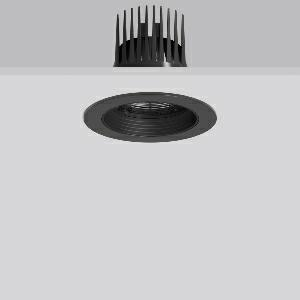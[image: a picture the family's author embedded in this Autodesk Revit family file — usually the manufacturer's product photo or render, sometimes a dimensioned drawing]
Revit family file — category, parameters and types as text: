
# Revit family: heledon_maxi_e_901769_003_c5fb
name_source: partatom
category: Lighting Fixtures
units: mm (PartAtom-declared; Revit-internal decimal feet)

## family parameters
Cut with Voids When Loaded = No
Host = Face
Light Source = No
Part Type = Normal
Room Calculation Point = No
Round Connector Dimension = Use Diameter
Shared = No

## types (1)
- HELEDON maxi E (1 x LED Modul 930, 3600 lm, 3000)
    Apparent Load = 35 VA
    Approval mark = CE
    CIE Flux Codes = 96 100 100 100 100
    Color Rendering = 90
    Color Temperature = 3000
    Default Elevation = 1800 mm
    Description = Series: HELEDON maxi
Round recessed downlight. Housing: die-cast aluminium, powder-coated. Black plastic ring and recessed LED to prevent glare from the side. Optical assembly with lens made of plastic (polycarbonate) for the best homogeneous light distribution - can be changed without tools. Best colour rendering index Ra>90. Suitable for Recessed ceiling mounting. Installation without tools thanks to spring fastening system. Including separate LED converter with connecting cable 600 mm.High quality converter without flickering and stroboscopic effect. Through-wiring box (5 pole) available as accessory. The following accessories can be mounted without use of tools: interchangeable lenses, decorative glasses, honeycomb louvre, clear and frosted diffusers, white interchangeable plastic ring. 
Colour: deep black, matt (RAL 9005)
Diameter: 162 mm
Height: 3 mm
Cut-out diameter: 152 mm
Recess height: 200 mm
Luminaire: recess height: 135 mm
Lamp: LED
Socket: without socket
Colour temperature: 3000K
Colour rendering index (CRI): 92
System power: 35 W
Rated luminous flux: 3600 lm
Luminous efficiency: 103 lm/W
Control gear: Regulated power supply
Protection class: II
Type of protection: IP 20
    Height = 0 mm  [stored 0 ft]
    Lamp = 1 x LED Modul 930
    Lamp Light Flux = 3600 lm
    Lamp count = 1
    Length = 162 mm
    Lifetime = 50000 h
    Luminous efficacy = 103 lm/W
    Manufacturer = RZB
    ModVariant = No
    Model = 901769.003
    Mounting Place = Ceiling
    Mounting Type = Recessed
    Number of Poles = 1
    OnlyDefault = Yes
    Power Factor = 1
    Product Name = HELEDON maxi E
    Product group = Recessed downlights
    ProductGroupID = 402
    Protection Class = Protection class II
    Protection Degree = IP 20
    RLX_Detail_Level = 1
    RLX_Emergency_Light_Flux = 0 lm
    RLX_Emergency_Type = 0
    RLX_Emergency_Type_DB = No
    RlxData = <blob elided: 124985 chars, md5=c5c26c8e>
    Socket = socket
    Standby Power = 0 W
    System Light Flux = 3600 lm
    System Power = 35 W
    Type Comments = Product without accessories
    Type Image = 901663.003.jpg
    URL = http://relux.com
    VarID = ---
    Voltage = 230 V
    Voltage Range = 220-240 V
    Weight = 0.00 kg
    Width = 0 mm  [stored 0 ft]

note: [stored X ft] marks values corroborated as IEEE doubles in the binary element streams (Revit-internal decimal feet)

## geometry (parser evidence)
native form markers: Blend x4, Sweep x11
no freeform markers — native parametric forms only
